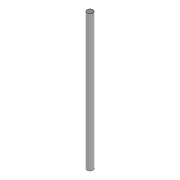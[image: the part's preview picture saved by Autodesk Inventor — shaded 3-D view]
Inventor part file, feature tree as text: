
AUTODESK INVENTOR PART (.ipt)
format: ipt  version: 2017 (Build 210142000, 142)  size: 69,632 bytes
history: native  units: mm
features: extrude x1, sketch x1
ambient origin geometry x8: Origin, YZ Plane, XZ Plane, XY Plane, X Axis, Y Axis, Z Axis, Center Point
bodies: Solid1 (feature_tree)
feature tree (2):
  extrude  "Extrusion1"  Depth=660.0mm TaperAngle=0.0deg
  sketch  "Sketch1"  dims[d0=30.0mm d1=660.0mm d2=0.0mm]
